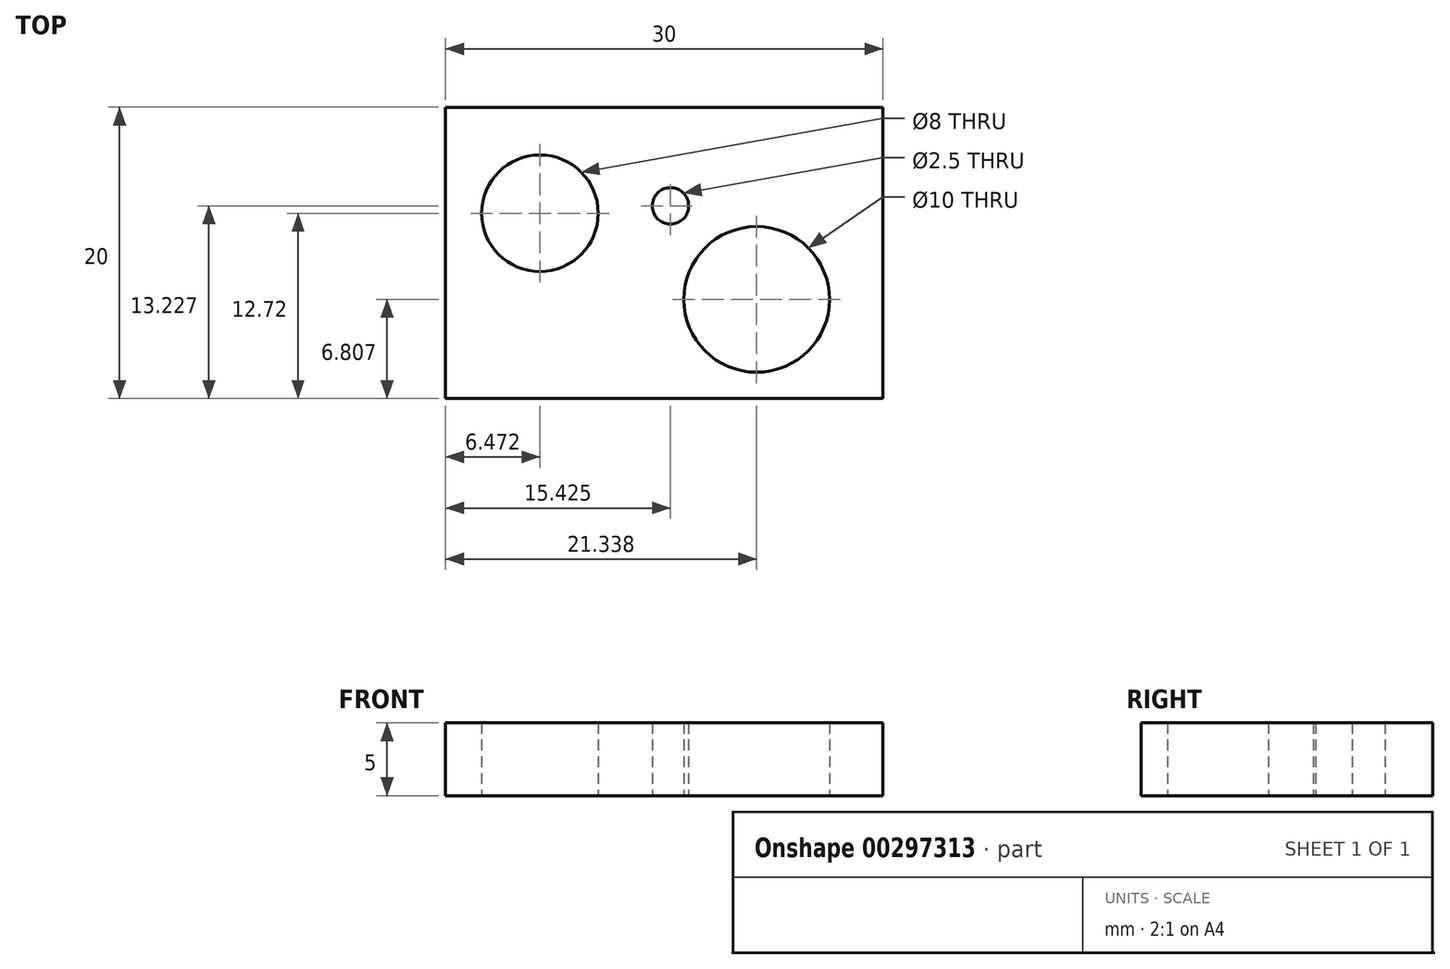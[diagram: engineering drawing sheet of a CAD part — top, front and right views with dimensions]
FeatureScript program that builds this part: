
annotation { "Feature Type Name" : "Feature", "Feature Type Description" : "" }
export const myFeature = defineFeature(function(context is Context, id is Id, definition is map)
    precondition{}
    {
        {
            var Q0;
            Q0=qCreatedBy(makeId("Top.planeOp"),FACE);
            var sketch = newSketch(context, id + "F0", { "sketchPlane" : qUnion([Q0])});
            skLineSegment(sketch, "E0.bottom", {"start": v(-13.55, 11.1) * mm, "end": v(16.45, 11.1) * mm});
            skLineSegment(sketch, "E0.top", {"start": v(-13.55, -8.9) * mm, "end": v(16.45, -8.9) * mm});
            skLineSegment(sketch, "E0.left", {"start": v(-13.55, 11.1) * mm, "end": v(-13.55, -8.9) * mm});
            skLineSegment(sketch, "E0.right", {"start": v(16.45, 11.1) * mm, "end": v(16.45, -8.9) * mm});
            skCircle(sketch, "E1", {"center": v(-7.08, 3.82) * mm, "radius": 4 * mm});
            skCircle(sketch, "E2", {"center": v(1.88, 4.33) * mm, "radius": 1.25 * mm});
            skCircle(sketch, "E3", {"center": v(7.79, -2.1) * mm, "radius": 5 * mm});
            skSolve(sketch);
        }
        {
            var Q0;
            Q0 = qSketchRegion(id + "F0", true);
            extrude(context, id + "F1", {"entities" : qUnion([Q0]), "depth" : 5 * mm});
        }
    });
